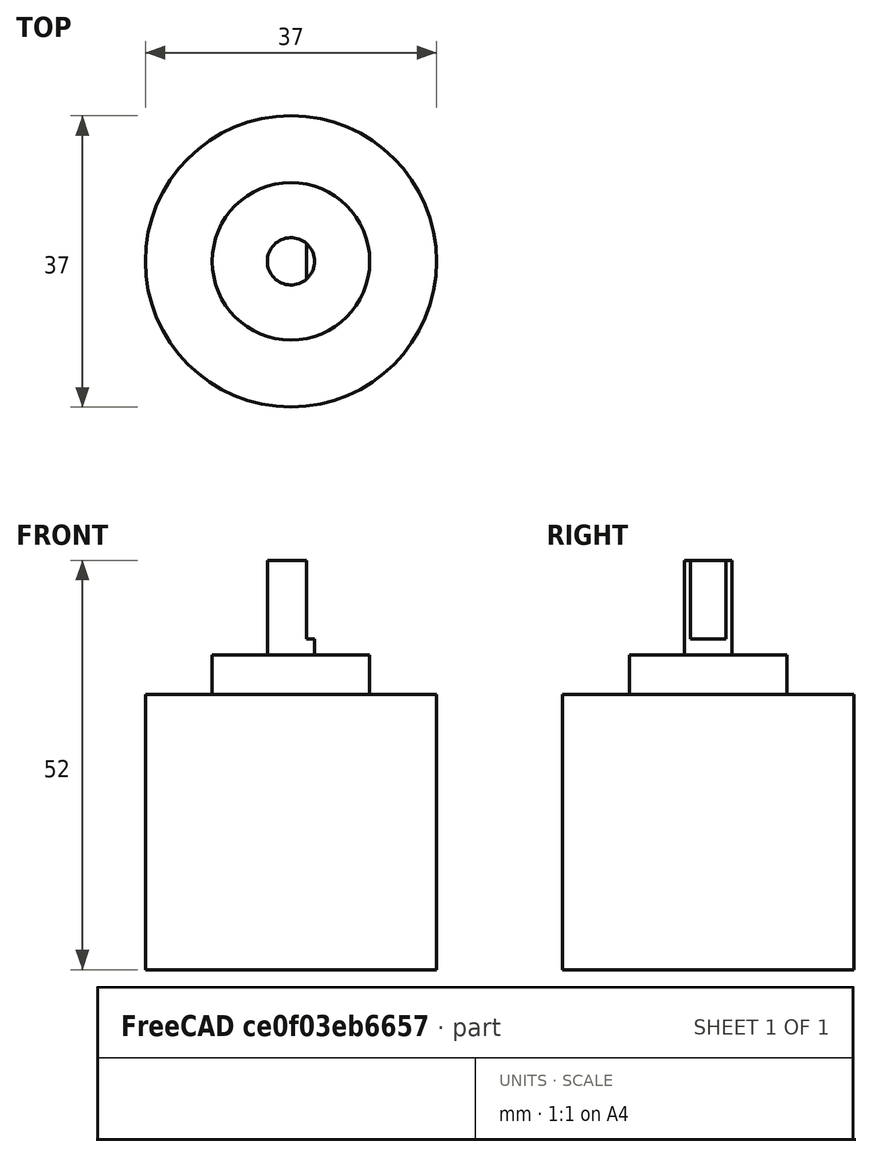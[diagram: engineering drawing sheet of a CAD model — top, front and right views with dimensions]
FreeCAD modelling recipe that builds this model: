
FCSTD DOCUMENT  (FreeCAD 0.17R13522 (Git))
Label: Rotary_Encoder_37mm
License: All rights reserved
LicenseURL: http://en.wikipedia.org/wiki/All_rights_reserved
objects: Part::Cylinder×3, Part::MultiFuse×1, Part::Box×1, Part::Cut×1
note: 6 computed .brp shape members not serialized (recipe doc carries the construction recipe); baked Part::Feature solids carry a one-line shape summary decoded from their .brp

FEATURE [Part::Cylinder] Cylinder
  Angle = 360
  AttacherType = Attacher::AttachEngine3D
  Height = 35
  Placement = pos=(0,0,-35) rot=(0,0,1;0rad)
  Radius = 18.5
FEATURE [Part::Cylinder] Cylinder001
  Angle = 360
  AttacherType = Attacher::AttachEngine3D
  Height = 5
  Radius = 10
FEATURE [Part::Cylinder] Cylinder002
  Angle = 360
  AttacherType = Attacher::AttachEngine3D
  Height = 12
  Placement = pos=(0,0,5) rot=(0,0,1;0rad)
  Radius = 3
FEATURE [Part::MultiFuse] Fusion  label="Positive Fusion"
  Shapes = -> [Cylinder,Cylinder001,Cylinder002]
FEATURE [Part::Box] Box  label="Cube"
  AttacherType = Attacher::AttachEngine3D
  Height = 10
  Length = 10
  Placement = pos=(2,-5,7) rot=(0,0,1;0rad)
  Width = 10
FEATURE [Part::Cut] Cut
  Base = -> Fusion
  Tool = -> Box
